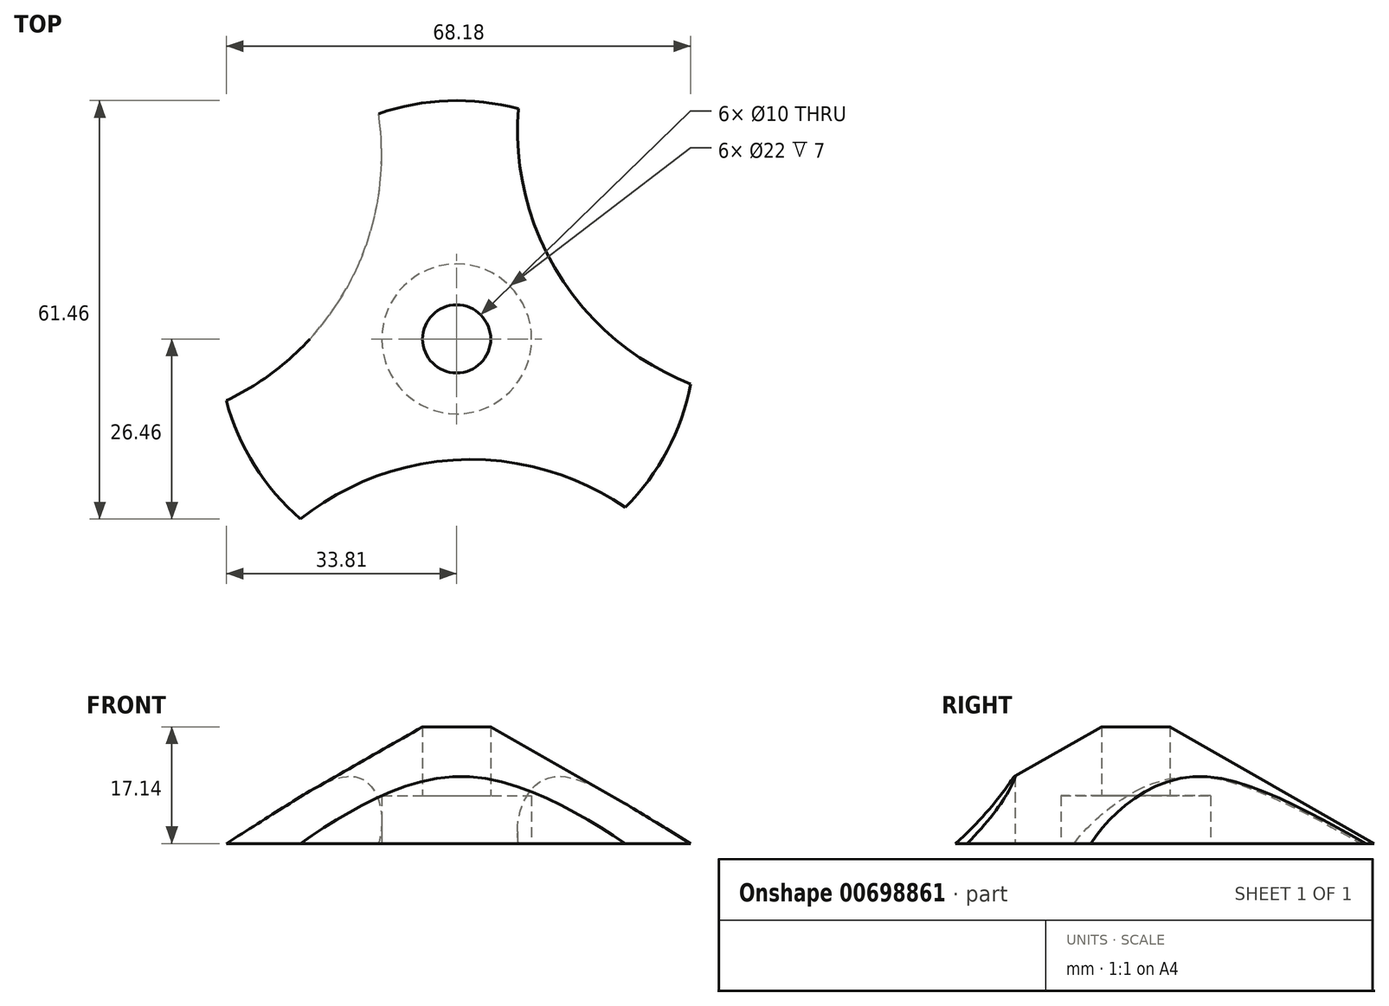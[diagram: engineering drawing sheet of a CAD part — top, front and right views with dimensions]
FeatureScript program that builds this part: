
annotation { "Feature Type Name" : "Feature", "Feature Type Description" : "" }
export const myFeature = defineFeature(function(context is Context, id is Id, definition is map)
    precondition{}
    {
        {
            var Q0;
            Q0=qCreatedBy(makeId("Front.planeOp"),FACE);
            var sketch = newSketch(context, id + "F0", { "sketchPlane" : qUnion([Q0])});
            skLineSegment(sketch, "E0", {"start": v(0, 0) * mm, "end": v(-35, 0) * mm});
            skLineSegment(sketch, "E1", {"start": v(-35, 0) * mm, "end": v(0, 20) * mm});
            skLineSegment(sketch, "E2", {"start": v(0, 20) * mm, "end": v(0, 0) * mm});
            skSolve(sketch);
        }
        {
            var Q0;
            Q0=makeQuery(id+"F0.imprint","IMPRINT",FACE,{"disambiguationData":[TD([[makeQuery(id+"F0.imprint","IMPRINT",EDGE,{"derivedFrom":sQuery(id+"F0.wireOp",EDGE,"E0")}),-1.0]])]});
            var Q1;
            Q1=sQuery(id+"F0.wireOp",EDGE,"E2");
            revolve(context, id + "F1", {"entities" : qUnion([Q0]), "axis" : qUnion([Q1]), "revolveType" : RevolveType.FULL});
        }
        {
            var Q0;
            Q0=qCreatedBy(makeId("Top.planeOp"),FACE);
            var sketch = newSketch(context, id + "F2", { "sketchPlane" : qUnion([Q0])});
            skCircle(sketch, "E3", {"center": v(2.07, -57.7) * mm, "radius": 40 * mm});
            skCircle(sketch, "E4", {"center": v(-51, 27.06) * mm, "radius": 40 * mm});
            skCircle(sketch, "E5", {"center": v(48.93, 30.64) * mm, "radius": 40 * mm});
            skLineSegment(sketch, "E6", {"start": v(2.07, -57.7) * mm, "end": v(-51, 27.06) * mm});
            skLineSegment(sketch, "E7", {"start": v(2.07, -57.7) * mm, "end": v(48.93, 30.64) * mm});
            skLineSegment(sketch, "E8", {"start": v(-51, 27.06) * mm, "end": v(48.93, 30.64) * mm});
            skLineSegment(sketch, "E9", {"start": v(2.07, -57.7) * mm, "end": v(0, 0) * mm});
            skLineSegment(sketch, "E10", {"start": v(48.93, 30.64) * mm, "end": v(0, 0) * mm});
            skLineSegment(sketch, "E11", {"start": v(0, 0) * mm, "end": v(-51, 27.06) * mm});
            skPoint(sketch, "E12", {"position": v(0, 0) * mm});
            skSolve(sketch);
        }
        {
            var Q0;
            {var subQ0=sQuery(id+"F2.wireOp",EDGE,"E7");var subQ1=sQuery(id+"F2.wireOp",EDGE,"E3");var subQ2=makeQuery(id+"F2.imprint","INTERSECT",VERTEX,{"derivedFrom":[subQ1,subQ0]});Q0=makeQuery(id+"F2.imprint","IMPRINT",FACE,{"disambiguationData":[TD([[makeQuery(id+"F2.imprint","IMPRINT",EDGE,{"disambiguationData":[TD([[subQ2,-1.0]])],"derivedFrom":subQ1}),1.0]])]});}
            var Q1;
            {var subQ0=sQuery(id+"F2.wireOp",EDGE,"E7");var subQ1=sQuery(id+"F2.wireOp",EDGE,"E3");var subQ2=makeQuery(id+"F2.imprint","INTERSECT",VERTEX,{"derivedFrom":[subQ1,subQ0]});Q1=makeQuery(id+"F2.imprint","IMPRINT",FACE,{"disambiguationData":[TD([[makeQuery(id+"F2.imprint","IMPRINT",EDGE,{"disambiguationData":[TD([[subQ2,1.0]])],"derivedFrom":subQ1}),1.0]])]});}
            var Q2;
            {var subQ0=sQuery(id+"F2.wireOp",EDGE,"E6");var subQ1=sQuery(id+"F2.wireOp",EDGE,"E3");var subQ2=makeQuery(id+"F2.imprint","INTERSECT",VERTEX,{"derivedFrom":[subQ1,subQ0]});Q2=makeQuery(id+"F2.imprint","IMPRINT",FACE,{"disambiguationData":[TD([[makeQuery(id+"F2.imprint","IMPRINT",EDGE,{"disambiguationData":[TD([[subQ2,1.0]])],"derivedFrom":subQ1}),1.0]])]});}
            var Q3;
            {var subQ0=sQuery(id+"F2.wireOp",EDGE,"E8");var subQ1=sQuery(id+"F2.wireOp",EDGE,"E5");var subQ2=makeQuery(id+"F2.imprint","INTERSECT",VERTEX,{"derivedFrom":[subQ1,subQ0]});Q3=makeQuery(id+"F2.imprint","IMPRINT",FACE,{"disambiguationData":[TD([[makeQuery(id+"F2.imprint","IMPRINT",EDGE,{"disambiguationData":[TD([[subQ2,1.0]])],"derivedFrom":subQ1}),1.0]])]});}
            var Q4;
            {var subQ0=sQuery(id+"F2.wireOp",EDGE,"E8");var subQ1=sQuery(id+"F2.wireOp",EDGE,"E5");var subQ2=makeQuery(id+"F2.imprint","INTERSECT",VERTEX,{"derivedFrom":[subQ1,subQ0]});Q4=makeQuery(id+"F2.imprint","IMPRINT",FACE,{"disambiguationData":[TD([[makeQuery(id+"F2.imprint","IMPRINT",EDGE,{"disambiguationData":[TD([[subQ2,-1.0]])],"derivedFrom":subQ1}),1.0]])]});}
            var Q5;
            {var subQ0=sQuery(id+"F2.wireOp",EDGE,"E7");var subQ1=sQuery(id+"F2.wireOp",EDGE,"E5");var subQ2=makeQuery(id+"F2.imprint","INTERSECT",VERTEX,{"derivedFrom":[subQ1,subQ0]});Q5=makeQuery(id+"F2.imprint","IMPRINT",FACE,{"disambiguationData":[TD([[makeQuery(id+"F2.imprint","IMPRINT",EDGE,{"disambiguationData":[TD([[subQ2,1.0]])],"derivedFrom":subQ1}),1.0]])]});}
            var Q6;
            {var subQ0=sQuery(id+"F2.wireOp",EDGE,"E6");var subQ1=sQuery(id+"F2.wireOp",EDGE,"E4");var subQ2=makeQuery(id+"F2.imprint","INTERSECT",VERTEX,{"derivedFrom":[subQ1,subQ0]});Q6=makeQuery(id+"F2.imprint","IMPRINT",FACE,{"disambiguationData":[TD([[makeQuery(id+"F2.imprint","IMPRINT",EDGE,{"disambiguationData":[TD([[subQ2,1.0]])],"derivedFrom":subQ1}),1.0]])]});}
            var Q7;
            {var subQ0=sQuery(id+"F2.wireOp",EDGE,"E8");var subQ1=sQuery(id+"F2.wireOp",EDGE,"E4");var subQ2=makeQuery(id+"F2.imprint","INTERSECT",VERTEX,{"derivedFrom":[subQ1,subQ0]});Q7=makeQuery(id+"F2.imprint","IMPRINT",FACE,{"disambiguationData":[TD([[makeQuery(id+"F2.imprint","IMPRINT",EDGE,{"disambiguationData":[TD([[subQ2,1.0]])],"derivedFrom":subQ1}),1.0]])]});}
            var Q8;
            {var subQ0=sQuery(id+"F2.wireOp",EDGE,"E6");var subQ1=sQuery(id+"F2.wireOp",EDGE,"E4");var subQ2=makeQuery(id+"F2.imprint","INTERSECT",VERTEX,{"derivedFrom":[subQ1,subQ0]});Q8=makeQuery(id+"F2.imprint","IMPRINT",FACE,{"disambiguationData":[TD([[makeQuery(id+"F2.imprint","IMPRINT",EDGE,{"disambiguationData":[TD([[subQ2,-1.0]])],"derivedFrom":subQ1}),1.0]])]});}
            extrude(context, id + "F3", {"entities" : qUnion([Q0, Q1, Q2, Q3, Q4, Q5, Q6, Q7, Q8]), "operationType" : NewBodyOperationType.REMOVE, "depth" : 25 * mm, "offsetDistance" : 25 * mm});
        }
        {
            var Q0;
            Q0=sQuery(id+"F2.wireOp",VERTEX,"E12");
            var Q1;
            Q1=makeQuery(id+"F1.opRevolve","SWEPT_BODY",BODY,{"disambiguationData":[OSD([sQuery(id+"F0.wireOp",EDGE,"E0"),sQuery(id+"F0.wireOp",EDGE,"E1"),sQuery(id+"F0.wireOp",EDGE,"E2")])]});
            hole(context, id + "F4", {"style" : HoleStyle.C_BORE, "endStyle" : HoleEndStyle.THROUGH, "oppositeDirection" : true, "holeDiameter" : 10 * mm, "cBoreDiameter" : 22 * mm, "cBoreDepth" : 7 * mm, "majorDiameter" : 5 * mm, "isTappedThrough" : true, "tappedDepth" : 12 * mm, "tapClearance" : 3, "startFromSketch" : true, "locations" : qUnion([Q0]), "scope" : qUnion([Q1])});
        }
    });
